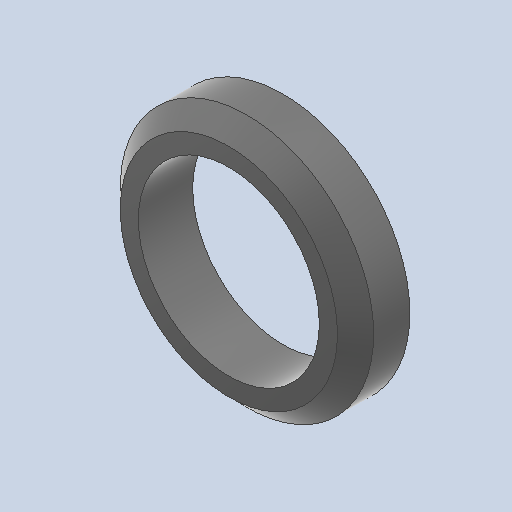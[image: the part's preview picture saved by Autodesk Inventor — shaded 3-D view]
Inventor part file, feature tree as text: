
AUTODESK INVENTOR PART (.ipt)
format: ipt  version: 2023 (Build 270158030, 158C)  size: 110,592 bytes
history: native  units: mm
features: other x3, sketch x1
ambient origin geometry x8: Origin, YZ Plane, XZ Plane, XY Plane, X Axis, Y Axis, Z Axis, Center Point
bodies: Solid1 (feature_tree)
feature tree (4):
  other  "w1.5f5-7n.ipt"
  other  "Solid1::w1.5f5-7n.ipt"
  other  "TaggingFeature1"
  sketch  "Sketch1"  dims[d0=10.0mm]
